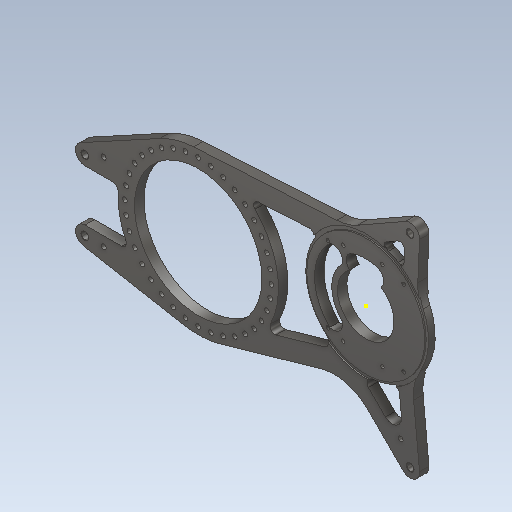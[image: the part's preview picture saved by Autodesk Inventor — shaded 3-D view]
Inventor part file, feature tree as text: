
AUTODESK INVENTOR PART (.ipt)
format: ipt  version: 2021 (Build 250183000, 183)  size: 581,632 bytes
history: native  units: in
note: dims shown in document units (in); Inventor stores cm internally (conversion verified against a paired STEP export)
features: sketch x17, extrude x11, hole x5, projected_geometry x3, chamfer x1
ambient origin geometry x8: Origin, YZ Plane, XZ Plane, XY Plane, X Axis, Y Axis, Z Axis, Center Point
bodies: Body1 (feature_tree)
feature tree (37):
  extrude  "Extrusion24"  Depth=2.16in
  extrude  "Extrusion28"  Depth=9.0in
  hole  "Hole9"  [1 undecoded]
  hole  "Hole11"  [1 undecoded]
  hole  "Hole13"  [1 undecoded]
  hole  "Hole14"  [1 undecoded]
  extrude  "Extrusion30"  Depth=0.5in
  extrude  "Extrusion31"  Depth=0.25in
  extrude  "Extrusion32"  Depth=7.75in
  extrude  "Extrusion33"  Depth=1.0in
  extrude  "Extrusion34"  Depth=1.0in
  chamfer  "Chamfer2"  Distance=0.1355in
  extrude  "Extrusion35"  Depth=0.5in
  extrude  "Extrusion37"  Depth=0.075in
  extrude  "Extrusion39"  Depth=0.075in
  sketch  "Sketch58"  dims[d318=1.0in]
  hole  "Hole15"  [1 undecoded]
  extrude  "Extrusion40"  Depth=0.75in
  sketch  "Sketch2"  dims[d9=8.5in d92=2.16in]
  sketch  "Sketch35"  dims[d118=0.75in d119=0.75in d120=0.75in d121=0.75in d137=9.0in d142=6.5in]
  projected_geometry  "Projected Loop2"
  sketch  "Sketch36"  dims[d143=1.0in d210=1.0in]
  sketch  "Sketch40"  dims[d211=6.0in d212=6.0in]
  sketch  "Sketch43"  dims[d213=3.718in d214=1.0in]
  sketch  "Sketch45"  dims[d235=10.718in d237=1.5in]
  sketch  "Sketch46"  dims[d239=0.5in d240=0.0in d266=6.75in]
  sketch  "Sketch47"  dims[d267=0.5in d268=0.0in]
  sketch  "Sketch48"  dims[d269=0.386in d270=0.75in d271=0.762in d272=0.25in d273=0.5635in d274=0.484in d275=0.8108in d288=5.0in]
  sketch  "Sketch49"  dims[d289=17.223in d290=7.75in]
  sketch  "Sketch50"  dims[d291=3.5433in d293=360.0deg]
  sketch  "Sketch53"  dims[d295=0.257in d296=0.75in d297=0.438in d298=0.25in d299=0.5635in d300=1.0in d301=0.8108in d302=0.1718in]
  sketch  "Sketch55"  dims[d303=15.0deg d316=1.0in]
  sketch  "Sketch57"  dims[d317=0.0481in]
  sketch  "Sketch59"  dims[d319=0.3972in]
  sketch  "Sketch60"  dims[d322=0.271in d323=0.1355in d324=0.5in d325=0.266in d326=0.75in d327=0.507in d328=0.25in d329=0.5635in d330=1.0in d331=0.8108in d332=0.5in d333=0.5in d334=0.5in d335=0.5in d336=0.5in d337=3.0in d338=5.0in d339=0.196in d340=0.5in d341=0.507in d342=0.25in d343=0.5635in d344=0.75in d345=0.0in d346=3.0in d347=1.0in d348=0.0in d349=0.75in d350=0.75in d351=0.5in d353=0.75in d354=0.75in d355=0.25in d356=1.0in d357=0.0in d358=0.25in d359=1.0in d360=0.0in d361=1.0in d362=1.0in d363=0.25in d364=1.0in d365=0.0in d366=2.5in d367=1.0in d368=0.0in d373=0.0156in d374=0.125in d375=45.0deg d376=6.65in d377=6.25in d378=0.075in d379=0.0in d381=1.1915in d382=2.3407in d383=0.878in d384=2.3407in d395=0.5in d396=0.5in d397=1.0in d398=0.0in d403=1.0in d404=0.0in d405=0.5in d406=0.5in d407=2.01in d408=2.01in d409=2.01in d410=2.01in d411=2.01in d412=2.01in d413=2.01in d414=2.01in d415=0.196in d416=0.5in d417=0.375in d418=0.25in d419=0.5635in d420=1.0in d421=0.8108in d422=6.029in d423=6.63in d424=0.075in d425=0.0in d429=0.3369in d430=0.878in d431=2.1978in]
  projected_geometry  "Project Cut Edges2"
  projected_geometry  "Project Cut Edges4"
note: 5 required parameter values undecoded (feature->parameter linkage not recoverable at this tier; creation-order binding heuristic only, values carry confidence <= 0.55)
